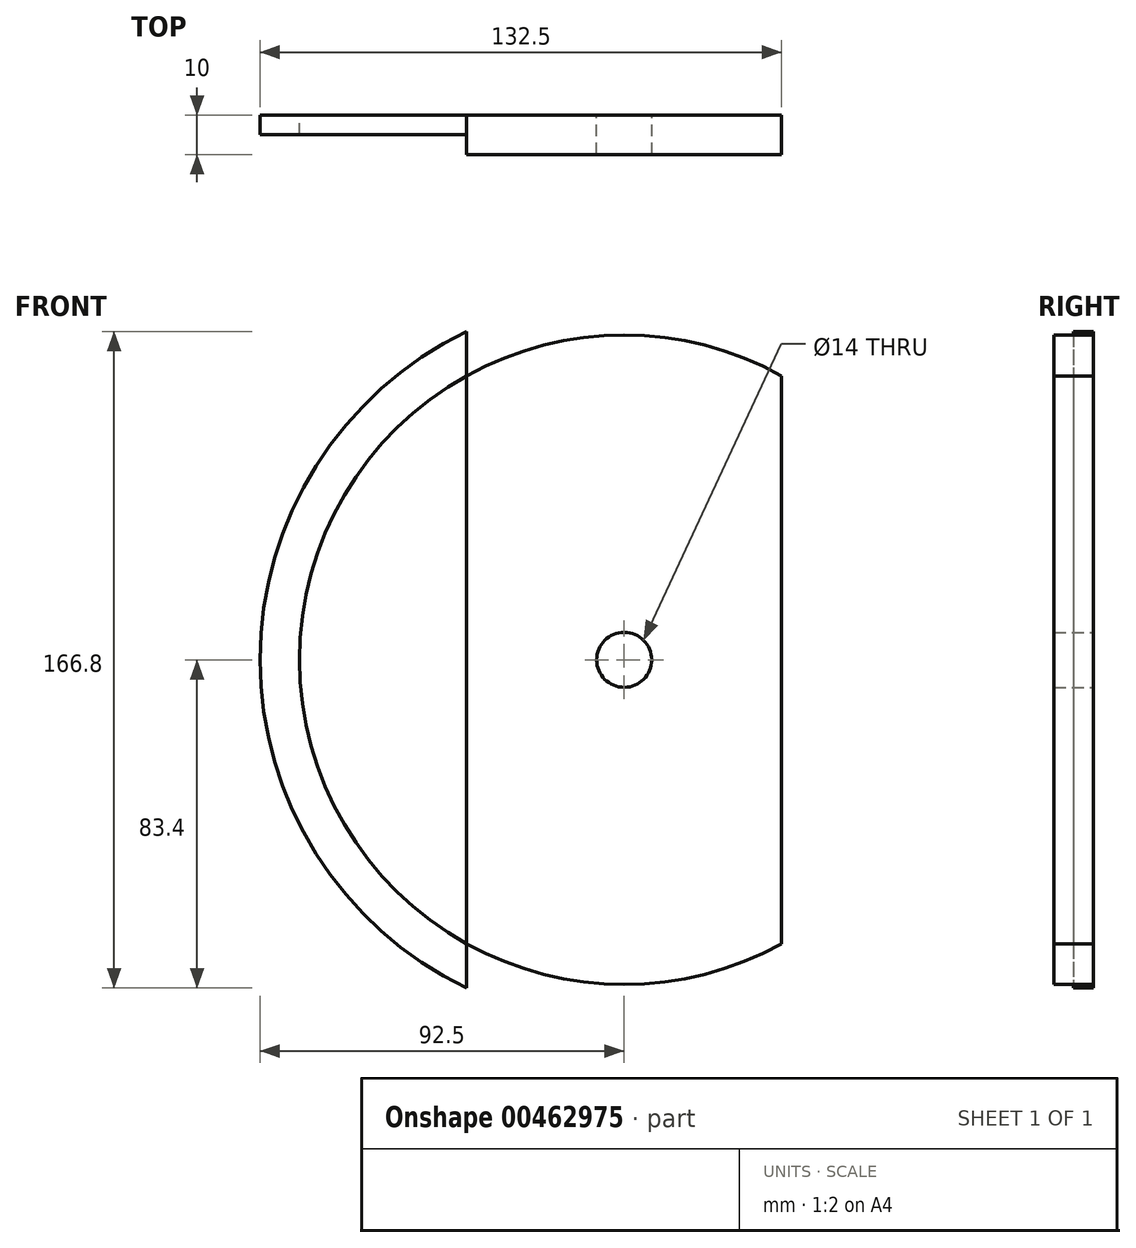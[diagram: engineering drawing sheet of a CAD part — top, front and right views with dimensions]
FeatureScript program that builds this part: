
annotation { "Feature Type Name" : "Feature", "Feature Type Description" : "" }
export const myFeature = defineFeature(function(context is Context, id is Id, definition is map)
    precondition{}
    {
        {
            var Q0;
            Q0=qCreatedBy(makeId("Front.planeOp"),FACE);
            var sketch = newSketch(context, id + "F0", { "sketchPlane" : qUnion([Q0])});
            skCircle(sketch, "E0", {"center": v(0, 0) * mm, "radius": 92.5 * mm});
            skCircle(sketch, "E1", {"center": v(0, 0) * mm, "radius": 82.5 * mm});
            skCircle(sketch, "E2", {"center": v(0, 0) * mm, "radius": 7 * mm});
            skLineSegment(sketch, "E3.bottom", {"start": v(-40, 105.58) * mm, "end": v(40, 105.58) * mm});
            skLineSegment(sketch, "E3.top", {"start": v(-40, -102.9) * mm, "end": v(40, -102.9) * mm});
            skLineSegment(sketch, "E3.left", {"start": v(-40, 105.58) * mm, "end": v(-40, -102.9) * mm});
            skLineSegment(sketch, "E3.right", {"start": v(40, 105.58) * mm, "end": v(40, -102.9) * mm});
            skSolve(sketch);
        }
        {
            var Q0;
            {var subQ0=sQuery(id+"F0.wireOp",EDGE,"E3.left");var subQ1=sQuery(id+"F0.wireOp",EDGE,"E0");var subQ2=makeQuery(id+"F0.imprint","INTERSECT",VERTEX,{"disambiguationData":[OD(0.0)],"derivedFrom":[subQ1,subQ0]});Q0=makeQuery(id+"F0.imprint","IMPRINT",FACE,{"disambiguationData":[TD([[makeQuery(id+"F0.imprint","IMPRINT",EDGE,{"disambiguationData":[TD([[subQ2,1.0]])],"derivedFrom":subQ1}),1.0]])]});}
            var Q1;
            {var subQ0=sQuery(id+"F0.wireOp",EDGE,"E3.left");var subQ1=sQuery(id+"F0.wireOp",EDGE,"E0");var subQ2=makeQuery(id+"F0.imprint","INTERSECT",VERTEX,{"disambiguationData":[OD(1.0)],"derivedFrom":[subQ1,subQ0]});Q1=makeQuery(id+"F0.imprint","IMPRINT",FACE,{"disambiguationData":[TD([[makeQuery(id+"F0.imprint","IMPRINT",EDGE,{"disambiguationData":[TD([[subQ2,-1.0]])],"derivedFrom":subQ1}),1.0]])]});}
            extrude(context, id + "F1", {"entities" : qUnion([Q0, Q1]), "depth" : 5 * mm});
        }
        {
            var Q0;
            Q0=makeQuery(id+"F0.imprint","IMPRINT",FACE,{"disambiguationData":[TD([[makeQuery(id+"F0.imprint","IMPRINT",EDGE,{"derivedFrom":sQuery(id+"F0.wireOp",EDGE,"E2")}),-1.0]])]});
            extrude(context, id + "F2", {"entities" : qUnion([Q0]), "depth" : 10 * mm});
        }
    });
